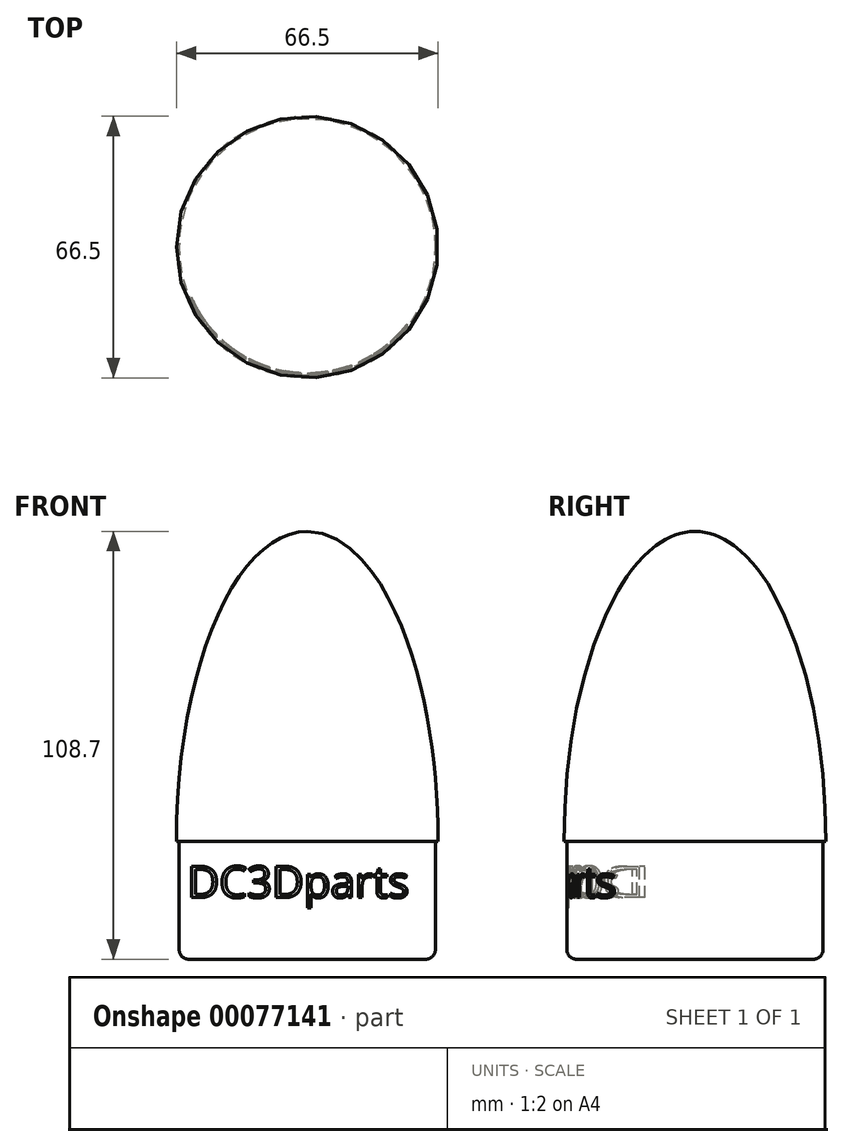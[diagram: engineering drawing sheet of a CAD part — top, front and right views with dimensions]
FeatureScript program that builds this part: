
annotation { "Feature Type Name" : "Feature", "Feature Type Description" : "" }
export const myFeature = defineFeature(function(context is Context, id is Id, definition is map)
    precondition{}
    {
        {
            var Q0;
            Q0=qCreatedBy(makeId("Front.planeOp"),FACE);
            var sketch = newSketch(context, id + "F0", { "sketchPlane" : qUnion([Q0])});
            skEllipticalArc(sketch, "E0", {});
            skLineSegment(sketch, "E1", {"start": v(0, 91.38) * mm, "end": v(0, -88.55) * mm, "construction": true});
            skPoint(sketch, "E1.startSnap0", {"position": v(0, 78.7) * mm});
            skLineSegment(sketch, "E2", {"start": v(-62.51, 0) * mm, "end": v(-32.55, 0) * mm, "construction": true});
            skLineSegment(sketch, "E3.top", {"start": v(0, -30) * mm, "end": v(-32.55, -30) * mm});
            skLineSegment(sketch, "E3.left", {"start": v(0, 0) * mm, "end": v(0, -30) * mm});
            skLineSegment(sketch, "E3.right", {"start": v(-32.55, 0) * mm, "end": v(-32.55, -30) * mm});
            skLineSegment(sketch, "E4", {"start": v(0, 78.7) * mm, "end": v(0, -30) * mm});
            skLineSegment(sketch, "E5.trimOffspring", {"start": v(0, 0) * mm, "end": v(63.8, 0) * mm, "construction": true});
            skLineSegment(sketch, "E6", {"start": v(-33.25, 0) * mm, "end": v(-32.55, 0) * mm});
            const initialGuessF0  = {"E0": [0, 0, 0, 1, 0.07870144238271146, 0.03325, 0, 1.5707963267948966]};
            skSetInitialGuess(sketch, initialGuessF0);
            skSolve(sketch);
        }
        {
            var Q0;
            {var subQ1=sQuery(id+"F0.wireOp",EDGE,"E0");Q0=makeQuery(id+"F0.imprint","IMPRINT",FACE,{"disambiguationData":[TD([[makeQuery(id+"F0.imprint","IMPRINT",EDGE,{"derivedFrom":subQ1}),1.0]])]});}
            var Q1;
            Q1=sQuery(id+"F0.wireOp",EDGE,"E1");
            revolve(context, id + "F1", {"entities" : qUnion([Q0]), "axis" : qUnion([Q1]), "revolveType" : RevolveType.FULL});
        }
        {
            var Q0;
            Q0=makeQuery(id+"F1.opRevolve","SWEPT_EDGE",EDGE,{"disambiguationData":[OSD([sQuery(id+"F0.wireOp",EDGE,"E3.top"),sQuery(id+"F0.wireOp",EDGE,"E3.right")])]});
            fillet(context, id + "F2", {"entities" : qUnion([Q0]), "radius" : 2.5 * mm, "tangentPropagation" : true, "allowEdgeOverflow" : false});
        }
        {
            var Q0;
            Q0=qCreatedBy(makeId("Front.planeOp"),FACE);
            cPlane(context, id + "F3", {"entities" : qUnion([Q0]), "cplaneType" : CPlaneType.OFFSET, "offset" : 40 * mm, "width" : 150 * mm, "height" : 150 * mm});
        }
        {
            var Q0;
            Q0=qCreatedBy(id+"F3.planeOp",FACE);
            var sketch = newSketch(context, id + "F4", { "sketchPlane" : qUnion([Q0])});
            skText(sketch, "E7", { "text": "DC3Dparts", "fontName": "OpenSans-Regular.ttf"});
            const initialGuessF4  = {"E7": [-0.03044, -0.01432, 1, 0, 0.008]};
            skSetInitialGuess(sketch, initialGuessF4);
            skSolve(sketch);
        }
        {
            var Q0;
            Q0=qCreatedBy(makeId("Front.planeOp"),FACE);
            var sketch = newSketch(context, id + "F5", { "sketchPlane" : qUnion([Q0])});
            skLineSegment(sketch, "E8.bottom", {"start": v(0, -18.53) * mm, "end": v(-32, -18.53) * mm});
            skLineSegment(sketch, "E8.top", {"start": v(0, -2.85) * mm, "end": v(-32, -2.85) * mm});
            skLineSegment(sketch, "E8.left", {"start": v(0, -18.53) * mm, "end": v(0, -2.85) * mm});
            skLineSegment(sketch, "E8.right", {"start": v(-32, -18.53) * mm, "end": v(-32, -2.85) * mm});
            skSolve(sketch);
        }
        {
            var Q0;
            Q0 = qSketchRegion(id + "F5", true);
            var Q1;
            Q1=sQuery(id+"F0.wireOp",EDGE,"E1");
            revolve(context, id + "F6", {"entities" : qUnion([Q0]), "axis" : qUnion([Q1]), "revolveType" : RevolveType.FULL});
        }
        {
            var Q0;
            Q0 = qSketchRegion(id + "F4", true);
            var Q1;
            Q1=qCreatedBy(makeId("Front.planeOp"),FACE);
            extrude(context, id + "F7", {"entities" : qUnion([Q0]), "endBound" : BoundingType.UP_TO_SURFACE, "oppositeDirection" : true, "depth" : 25 * mm, "endBoundEntityFace" : qUnion([Q1]), "offsetDistance" : 25 * mm});
        }
        {
            var Q0;
            Q0=makeQuery(id+"F6.opRevolve","SWEPT_BODY",BODY,{"disambiguationData":[OSD([sQuery(id+"F5.wireOp",EDGE,"E8.bottom"),sQuery(id+"F5.wireOp",EDGE,"E8.top"),sQuery(id+"F5.wireOp",EDGE,"E8.left"),sQuery(id+"F5.wireOp",EDGE,"E8.right")])]});
            var Q1;
            Q1=makeQuery(id+"F7.opExtrude","SWEPT_BODY",BODY,{"disambiguationData":[OSD([sQuery(id+"F4.wireOp",EDGE,"E7.sketch_text.stroke-0"),sQuery(id+"F4.wireOp",EDGE,"E7.sketch_text.stroke-1"),sQuery(id+"F4.wireOp",EDGE,"E7.sketch_text.stroke-2"),sQuery(id+"F4.wireOp",EDGE,"E7.sketch_text.stroke-3"),sQuery(id+"F4.wireOp",EDGE,"E7.sketch_text.stroke-4"),sQuery(id+"F4.wireOp",EDGE,"E7.sketch_text.stroke-5"),sQuery(id+"F4.wireOp",EDGE,"E7.sketch_text.stroke-6"),sQuery(id+"F4.wireOp",EDGE,"E7.sketch_text.stroke-7"),sQuery(id+"F4.wireOp",EDGE,"E7.sketch_text.stroke-8"),sQuery(id+"F4.wireOp",EDGE,"E7.sketch_text.stroke-9"),sQuery(id+"F4.wireOp",EDGE,"E7.sketch_text.stroke-10"),sQuery(id+"F4.wireOp",EDGE,"E7.sketch_text.stroke-11"),sQuery(id+"F4.wireOp",EDGE,"E7.sketch_text.stroke-12"),sQuery(id+"F4.wireOp",EDGE,"E7.sketch_text.stroke-13")])]});
            var Q2;
            Q2=makeQuery(id+"F7.opExtrude","SWEPT_BODY",BODY,{"disambiguationData":[OSD([sQuery(id+"F4.wireOp",EDGE,"E7.sketch_text.stroke-14"),sQuery(id+"F4.wireOp",EDGE,"E7.sketch_text.stroke-15"),sQuery(id+"F4.wireOp",EDGE,"E7.sketch_text.stroke-16"),sQuery(id+"F4.wireOp",EDGE,"E7.sketch_text.stroke-17"),sQuery(id+"F4.wireOp",EDGE,"E7.sketch_text.stroke-18"),sQuery(id+"F4.wireOp",EDGE,"E7.sketch_text.stroke-19"),sQuery(id+"F4.wireOp",EDGE,"E7.sketch_text.stroke-20"),sQuery(id+"F4.wireOp",EDGE,"E7.sketch_text.stroke-21"),sQuery(id+"F4.wireOp",EDGE,"E7.sketch_text.stroke-22"),sQuery(id+"F4.wireOp",EDGE,"E7.sketch_text.stroke-23"),sQuery(id+"F4.wireOp",EDGE,"E7.sketch_text.stroke-24"),sQuery(id+"F4.wireOp",EDGE,"E7.sketch_text.stroke-25"),sQuery(id+"F4.wireOp",EDGE,"E7.sketch_text.stroke-26"),sQuery(id+"F4.wireOp",EDGE,"E7.sketch_text.stroke-27"),sQuery(id+"F4.wireOp",EDGE,"E7.sketch_text.stroke-28")])]});
            var Q3;
            Q3=makeQuery(id+"F7.opExtrude","SWEPT_BODY",BODY,{"disambiguationData":[OSD([sQuery(id+"F4.wireOp",EDGE,"E7.sketch_text.stroke-29"),sQuery(id+"F4.wireOp",EDGE,"E7.sketch_text.stroke-30"),sQuery(id+"F4.wireOp",EDGE,"E7.sketch_text.stroke-31"),sQuery(id+"F4.wireOp",EDGE,"E7.sketch_text.stroke-32"),sQuery(id+"F4.wireOp",EDGE,"E7.sketch_text.stroke-33"),sQuery(id+"F4.wireOp",EDGE,"E7.sketch_text.stroke-34"),sQuery(id+"F4.wireOp",EDGE,"E7.sketch_text.stroke-35"),sQuery(id+"F4.wireOp",EDGE,"E7.sketch_text.stroke-36"),sQuery(id+"F4.wireOp",EDGE,"E7.sketch_text.stroke-37"),sQuery(id+"F4.wireOp",EDGE,"E7.sketch_text.stroke-38"),sQuery(id+"F4.wireOp",EDGE,"E7.sketch_text.stroke-39"),sQuery(id+"F4.wireOp",EDGE,"E7.sketch_text.stroke-40"),sQuery(id+"F4.wireOp",EDGE,"E7.sketch_text.stroke-41"),sQuery(id+"F4.wireOp",EDGE,"E7.sketch_text.stroke-42"),sQuery(id+"F4.wireOp",EDGE,"E7.sketch_text.stroke-43"),sQuery(id+"F4.wireOp",EDGE,"E7.sketch_text.stroke-44"),sQuery(id+"F4.wireOp",EDGE,"E7.sketch_text.stroke-45"),sQuery(id+"F4.wireOp",EDGE,"E7.sketch_text.stroke-46"),sQuery(id+"F4.wireOp",EDGE,"E7.sketch_text.stroke-47"),sQuery(id+"F4.wireOp",EDGE,"E7.sketch_text.stroke-48"),sQuery(id+"F4.wireOp",EDGE,"E7.sketch_text.stroke-49"),sQuery(id+"F4.wireOp",EDGE,"E7.sketch_text.stroke-50"),sQuery(id+"F4.wireOp",EDGE,"E7.sketch_text.stroke-51"),sQuery(id+"F4.wireOp",EDGE,"E7.sketch_text.stroke-52"),sQuery(id+"F4.wireOp",EDGE,"E7.sketch_text.stroke-53"),sQuery(id+"F4.wireOp",EDGE,"E7.sketch_text.stroke-54"),sQuery(id+"F4.wireOp",EDGE,"E7.sketch_text.stroke-55"),sQuery(id+"F4.wireOp",EDGE,"E7.sketch_text.stroke-56")])]});
            var Q4;
            Q4=makeQuery(id+"F7.opExtrude","SWEPT_BODY",BODY,{"disambiguationData":[OSD([sQuery(id+"F4.wireOp",EDGE,"E7.sketch_text.stroke-57"),sQuery(id+"F4.wireOp",EDGE,"E7.sketch_text.stroke-58"),sQuery(id+"F4.wireOp",EDGE,"E7.sketch_text.stroke-59"),sQuery(id+"F4.wireOp",EDGE,"E7.sketch_text.stroke-60"),sQuery(id+"F4.wireOp",EDGE,"E7.sketch_text.stroke-61"),sQuery(id+"F4.wireOp",EDGE,"E7.sketch_text.stroke-62"),sQuery(id+"F4.wireOp",EDGE,"E7.sketch_text.stroke-63"),sQuery(id+"F4.wireOp",EDGE,"E7.sketch_text.stroke-64"),sQuery(id+"F4.wireOp",EDGE,"E7.sketch_text.stroke-65"),sQuery(id+"F4.wireOp",EDGE,"E7.sketch_text.stroke-66"),sQuery(id+"F4.wireOp",EDGE,"E7.sketch_text.stroke-67"),sQuery(id+"F4.wireOp",EDGE,"E7.sketch_text.stroke-68"),sQuery(id+"F4.wireOp",EDGE,"E7.sketch_text.stroke-69"),sQuery(id+"F4.wireOp",EDGE,"E7.sketch_text.stroke-70")])]});
            var Q5;
            Q5=makeQuery(id+"F7.opExtrude","SWEPT_BODY",BODY,{"disambiguationData":[OSD([sQuery(id+"F4.wireOp",EDGE,"E7.sketch_text.stroke-71"),sQuery(id+"F4.wireOp",EDGE,"E7.sketch_text.stroke-72"),sQuery(id+"F4.wireOp",EDGE,"E7.sketch_text.stroke-73"),sQuery(id+"F4.wireOp",EDGE,"E7.sketch_text.stroke-74"),sQuery(id+"F4.wireOp",EDGE,"E7.sketch_text.stroke-75"),sQuery(id+"F4.wireOp",EDGE,"E7.sketch_text.stroke-76"),sQuery(id+"F4.wireOp",EDGE,"E7.sketch_text.stroke-77"),sQuery(id+"F4.wireOp",EDGE,"E7.sketch_text.stroke-78"),sQuery(id+"F4.wireOp",EDGE,"E7.sketch_text.stroke-79"),sQuery(id+"F4.wireOp",EDGE,"E7.sketch_text.stroke-80"),sQuery(id+"F4.wireOp",EDGE,"E7.sketch_text.stroke-81"),sQuery(id+"F4.wireOp",EDGE,"E7.sketch_text.stroke-82"),sQuery(id+"F4.wireOp",EDGE,"E7.sketch_text.stroke-83"),sQuery(id+"F4.wireOp",EDGE,"E7.sketch_text.stroke-84"),sQuery(id+"F4.wireOp",EDGE,"E7.sketch_text.stroke-85"),sQuery(id+"F4.wireOp",EDGE,"E7.sketch_text.stroke-86"),sQuery(id+"F4.wireOp",EDGE,"E7.sketch_text.stroke-87"),sQuery(id+"F4.wireOp",EDGE,"E7.sketch_text.stroke-88"),sQuery(id+"F4.wireOp",EDGE,"E7.sketch_text.stroke-89"),sQuery(id+"F4.wireOp",EDGE,"E7.sketch_text.stroke-90"),sQuery(id+"F4.wireOp",EDGE,"E7.sketch_text.stroke-91"),sQuery(id+"F4.wireOp",EDGE,"E7.sketch_text.stroke-92"),sQuery(id+"F4.wireOp",EDGE,"E7.sketch_text.stroke-93"),sQuery(id+"F4.wireOp",EDGE,"E7.sketch_text.stroke-94"),sQuery(id+"F4.wireOp",EDGE,"E7.sketch_text.stroke-95")])]});
            var Q6;
            Q6=makeQuery(id+"F7.opExtrude","SWEPT_BODY",BODY,{"disambiguationData":[OSD([sQuery(id+"F4.wireOp",EDGE,"E7.sketch_text.stroke-96"),sQuery(id+"F4.wireOp",EDGE,"E7.sketch_text.stroke-97"),sQuery(id+"F4.wireOp",EDGE,"E7.sketch_text.stroke-98"),sQuery(id+"F4.wireOp",EDGE,"E7.sketch_text.stroke-99"),sQuery(id+"F4.wireOp",EDGE,"E7.sketch_text.stroke-100"),sQuery(id+"F4.wireOp",EDGE,"E7.sketch_text.stroke-101"),sQuery(id+"F4.wireOp",EDGE,"E7.sketch_text.stroke-102"),sQuery(id+"F4.wireOp",EDGE,"E7.sketch_text.stroke-103"),sQuery(id+"F4.wireOp",EDGE,"E7.sketch_text.stroke-104"),sQuery(id+"F4.wireOp",EDGE,"E7.sketch_text.stroke-105"),sQuery(id+"F4.wireOp",EDGE,"E7.sketch_text.stroke-106"),sQuery(id+"F4.wireOp",EDGE,"E7.sketch_text.stroke-107"),sQuery(id+"F4.wireOp",EDGE,"E7.sketch_text.stroke-108"),sQuery(id+"F4.wireOp",EDGE,"E7.sketch_text.stroke-109"),sQuery(id+"F4.wireOp",EDGE,"E7.sketch_text.stroke-110"),sQuery(id+"F4.wireOp",EDGE,"E7.sketch_text.stroke-111"),sQuery(id+"F4.wireOp",EDGE,"E7.sketch_text.stroke-112"),sQuery(id+"F4.wireOp",EDGE,"E7.sketch_text.stroke-113"),sQuery(id+"F4.wireOp",EDGE,"E7.sketch_text.stroke-114"),sQuery(id+"F4.wireOp",EDGE,"E7.sketch_text.stroke-115"),sQuery(id+"F4.wireOp",EDGE,"E7.sketch_text.stroke-116"),sQuery(id+"F4.wireOp",EDGE,"E7.sketch_text.stroke-117"),sQuery(id+"F4.wireOp",EDGE,"E7.sketch_text.stroke-118"),sQuery(id+"F4.wireOp",EDGE,"E7.sketch_text.stroke-119"),sQuery(id+"F4.wireOp",EDGE,"E7.sketch_text.stroke-120"),sQuery(id+"F4.wireOp",EDGE,"E7.sketch_text.stroke-121"),sQuery(id+"F4.wireOp",EDGE,"E7.sketch_text.stroke-122")])]});
            var Q7;
            Q7=makeQuery(id+"F7.opExtrude","SWEPT_BODY",BODY,{"disambiguationData":[OSD([sQuery(id+"F4.wireOp",EDGE,"E7.sketch_text.stroke-123"),sQuery(id+"F4.wireOp",EDGE,"E7.sketch_text.stroke-124"),sQuery(id+"F4.wireOp",EDGE,"E7.sketch_text.stroke-125"),sQuery(id+"F4.wireOp",EDGE,"E7.sketch_text.stroke-126"),sQuery(id+"F4.wireOp",EDGE,"E7.sketch_text.stroke-127"),sQuery(id+"F4.wireOp",EDGE,"E7.sketch_text.stroke-128"),sQuery(id+"F4.wireOp",EDGE,"E7.sketch_text.stroke-129"),sQuery(id+"F4.wireOp",EDGE,"E7.sketch_text.stroke-130"),sQuery(id+"F4.wireOp",EDGE,"E7.sketch_text.stroke-131"),sQuery(id+"F4.wireOp",EDGE,"E7.sketch_text.stroke-132"),sQuery(id+"F4.wireOp",EDGE,"E7.sketch_text.stroke-133"),sQuery(id+"F4.wireOp",EDGE,"E7.sketch_text.stroke-134"),sQuery(id+"F4.wireOp",EDGE,"E7.sketch_text.stroke-135")])]});
            var Q8;
            Q8=makeQuery(id+"F7.opExtrude","SWEPT_BODY",BODY,{"disambiguationData":[OSD([sQuery(id+"F4.wireOp",EDGE,"E7.sketch_text.stroke-136"),sQuery(id+"F4.wireOp",EDGE,"E7.sketch_text.stroke-137"),sQuery(id+"F4.wireOp",EDGE,"E7.sketch_text.stroke-138"),sQuery(id+"F4.wireOp",EDGE,"E7.sketch_text.stroke-139"),sQuery(id+"F4.wireOp",EDGE,"E7.sketch_text.stroke-140"),sQuery(id+"F4.wireOp",EDGE,"E7.sketch_text.stroke-141"),sQuery(id+"F4.wireOp",EDGE,"E7.sketch_text.stroke-142"),sQuery(id+"F4.wireOp",EDGE,"E7.sketch_text.stroke-143"),sQuery(id+"F4.wireOp",EDGE,"E7.sketch_text.stroke-144"),sQuery(id+"F4.wireOp",EDGE,"E7.sketch_text.stroke-145"),sQuery(id+"F4.wireOp",EDGE,"E7.sketch_text.stroke-146"),sQuery(id+"F4.wireOp",EDGE,"E7.sketch_text.stroke-147"),sQuery(id+"F4.wireOp",EDGE,"E7.sketch_text.stroke-148"),sQuery(id+"F4.wireOp",EDGE,"E7.sketch_text.stroke-149"),sQuery(id+"F4.wireOp",EDGE,"E7.sketch_text.stroke-150"),sQuery(id+"F4.wireOp",EDGE,"E7.sketch_text.stroke-151"),sQuery(id+"F4.wireOp",EDGE,"E7.sketch_text.stroke-152"),sQuery(id+"F4.wireOp",EDGE,"E7.sketch_text.stroke-153"),sQuery(id+"F4.wireOp",EDGE,"E7.sketch_text.stroke-154")])]});
            var Q9;
            Q9=makeQuery(id+"F7.opExtrude","SWEPT_BODY",BODY,{"disambiguationData":[OSD([sQuery(id+"F4.wireOp",EDGE,"E7.sketch_text.stroke-155"),sQuery(id+"F4.wireOp",EDGE,"E7.sketch_text.stroke-156"),sQuery(id+"F4.wireOp",EDGE,"E7.sketch_text.stroke-157"),sQuery(id+"F4.wireOp",EDGE,"E7.sketch_text.stroke-158"),sQuery(id+"F4.wireOp",EDGE,"E7.sketch_text.stroke-159"),sQuery(id+"F4.wireOp",EDGE,"E7.sketch_text.stroke-160"),sQuery(id+"F4.wireOp",EDGE,"E7.sketch_text.stroke-161"),sQuery(id+"F4.wireOp",EDGE,"E7.sketch_text.stroke-162"),sQuery(id+"F4.wireOp",EDGE,"E7.sketch_text.stroke-163"),sQuery(id+"F4.wireOp",EDGE,"E7.sketch_text.stroke-164"),sQuery(id+"F4.wireOp",EDGE,"E7.sketch_text.stroke-165"),sQuery(id+"F4.wireOp",EDGE,"E7.sketch_text.stroke-166"),sQuery(id+"F4.wireOp",EDGE,"E7.sketch_text.stroke-167"),sQuery(id+"F4.wireOp",EDGE,"E7.sketch_text.stroke-168"),sQuery(id+"F4.wireOp",EDGE,"E7.sketch_text.stroke-169"),sQuery(id+"F4.wireOp",EDGE,"E7.sketch_text.stroke-170"),sQuery(id+"F4.wireOp",EDGE,"E7.sketch_text.stroke-171"),sQuery(id+"F4.wireOp",EDGE,"E7.sketch_text.stroke-172"),sQuery(id+"F4.wireOp",EDGE,"E7.sketch_text.stroke-173"),sQuery(id+"F4.wireOp",EDGE,"E7.sketch_text.stroke-174"),sQuery(id+"F4.wireOp",EDGE,"E7.sketch_text.stroke-175"),sQuery(id+"F4.wireOp",EDGE,"E7.sketch_text.stroke-176"),sQuery(id+"F4.wireOp",EDGE,"E7.sketch_text.stroke-177"),sQuery(id+"F4.wireOp",EDGE,"E7.sketch_text.stroke-178"),sQuery(id+"F4.wireOp",EDGE,"E7.sketch_text.stroke-179")])]});
            booleanBodies(context, id + "F8", {"operationType" : BooleanOperationType.SUBTRACTION, "tools" : qUnion([Q0]), "targets" : qUnion([Q1, Q2, Q3, Q4, Q5, Q6, Q7, Q8, Q9])});
        }
        {
            var Q0;
            Q0=makeQuery(id+"F7.opExtrude","SWEPT_BODY",BODY,{"disambiguationData":[OSD([sQuery(id+"F4.wireOp",EDGE,"E7.sketch_text.stroke-0"),sQuery(id+"F4.wireOp",EDGE,"E7.sketch_text.stroke-1"),sQuery(id+"F4.wireOp",EDGE,"E7.sketch_text.stroke-2"),sQuery(id+"F4.wireOp",EDGE,"E7.sketch_text.stroke-3"),sQuery(id+"F4.wireOp",EDGE,"E7.sketch_text.stroke-4"),sQuery(id+"F4.wireOp",EDGE,"E7.sketch_text.stroke-5"),sQuery(id+"F4.wireOp",EDGE,"E7.sketch_text.stroke-6"),sQuery(id+"F4.wireOp",EDGE,"E7.sketch_text.stroke-7"),sQuery(id+"F4.wireOp",EDGE,"E7.sketch_text.stroke-8"),sQuery(id+"F4.wireOp",EDGE,"E7.sketch_text.stroke-9"),sQuery(id+"F4.wireOp",EDGE,"E7.sketch_text.stroke-10"),sQuery(id+"F4.wireOp",EDGE,"E7.sketch_text.stroke-11"),sQuery(id+"F4.wireOp",EDGE,"E7.sketch_text.stroke-12"),sQuery(id+"F4.wireOp",EDGE,"E7.sketch_text.stroke-13")])]});
            var Q1;
            Q1=makeQuery(id+"F7.opExtrude","SWEPT_BODY",BODY,{"disambiguationData":[OSD([sQuery(id+"F4.wireOp",EDGE,"E7.sketch_text.stroke-14"),sQuery(id+"F4.wireOp",EDGE,"E7.sketch_text.stroke-15"),sQuery(id+"F4.wireOp",EDGE,"E7.sketch_text.stroke-16"),sQuery(id+"F4.wireOp",EDGE,"E7.sketch_text.stroke-17"),sQuery(id+"F4.wireOp",EDGE,"E7.sketch_text.stroke-18"),sQuery(id+"F4.wireOp",EDGE,"E7.sketch_text.stroke-19"),sQuery(id+"F4.wireOp",EDGE,"E7.sketch_text.stroke-20"),sQuery(id+"F4.wireOp",EDGE,"E7.sketch_text.stroke-21"),sQuery(id+"F4.wireOp",EDGE,"E7.sketch_text.stroke-22"),sQuery(id+"F4.wireOp",EDGE,"E7.sketch_text.stroke-23"),sQuery(id+"F4.wireOp",EDGE,"E7.sketch_text.stroke-24"),sQuery(id+"F4.wireOp",EDGE,"E7.sketch_text.stroke-25"),sQuery(id+"F4.wireOp",EDGE,"E7.sketch_text.stroke-26"),sQuery(id+"F4.wireOp",EDGE,"E7.sketch_text.stroke-27"),sQuery(id+"F4.wireOp",EDGE,"E7.sketch_text.stroke-28")])]});
            var Q2;
            Q2=makeQuery(id+"F7.opExtrude","SWEPT_BODY",BODY,{"disambiguationData":[OSD([sQuery(id+"F4.wireOp",EDGE,"E7.sketch_text.stroke-29"),sQuery(id+"F4.wireOp",EDGE,"E7.sketch_text.stroke-30"),sQuery(id+"F4.wireOp",EDGE,"E7.sketch_text.stroke-31"),sQuery(id+"F4.wireOp",EDGE,"E7.sketch_text.stroke-32"),sQuery(id+"F4.wireOp",EDGE,"E7.sketch_text.stroke-33"),sQuery(id+"F4.wireOp",EDGE,"E7.sketch_text.stroke-34"),sQuery(id+"F4.wireOp",EDGE,"E7.sketch_text.stroke-35"),sQuery(id+"F4.wireOp",EDGE,"E7.sketch_text.stroke-36"),sQuery(id+"F4.wireOp",EDGE,"E7.sketch_text.stroke-37"),sQuery(id+"F4.wireOp",EDGE,"E7.sketch_text.stroke-38"),sQuery(id+"F4.wireOp",EDGE,"E7.sketch_text.stroke-39"),sQuery(id+"F4.wireOp",EDGE,"E7.sketch_text.stroke-40"),sQuery(id+"F4.wireOp",EDGE,"E7.sketch_text.stroke-41"),sQuery(id+"F4.wireOp",EDGE,"E7.sketch_text.stroke-42"),sQuery(id+"F4.wireOp",EDGE,"E7.sketch_text.stroke-43"),sQuery(id+"F4.wireOp",EDGE,"E7.sketch_text.stroke-44"),sQuery(id+"F4.wireOp",EDGE,"E7.sketch_text.stroke-45"),sQuery(id+"F4.wireOp",EDGE,"E7.sketch_text.stroke-46"),sQuery(id+"F4.wireOp",EDGE,"E7.sketch_text.stroke-47"),sQuery(id+"F4.wireOp",EDGE,"E7.sketch_text.stroke-48"),sQuery(id+"F4.wireOp",EDGE,"E7.sketch_text.stroke-49"),sQuery(id+"F4.wireOp",EDGE,"E7.sketch_text.stroke-50"),sQuery(id+"F4.wireOp",EDGE,"E7.sketch_text.stroke-51"),sQuery(id+"F4.wireOp",EDGE,"E7.sketch_text.stroke-52"),sQuery(id+"F4.wireOp",EDGE,"E7.sketch_text.stroke-53"),sQuery(id+"F4.wireOp",EDGE,"E7.sketch_text.stroke-54"),sQuery(id+"F4.wireOp",EDGE,"E7.sketch_text.stroke-55"),sQuery(id+"F4.wireOp",EDGE,"E7.sketch_text.stroke-56")])]});
            var Q3;
            Q3=makeQuery(id+"F7.opExtrude","SWEPT_BODY",BODY,{"disambiguationData":[OSD([sQuery(id+"F4.wireOp",EDGE,"E7.sketch_text.stroke-57"),sQuery(id+"F4.wireOp",EDGE,"E7.sketch_text.stroke-58"),sQuery(id+"F4.wireOp",EDGE,"E7.sketch_text.stroke-59"),sQuery(id+"F4.wireOp",EDGE,"E7.sketch_text.stroke-60"),sQuery(id+"F4.wireOp",EDGE,"E7.sketch_text.stroke-61"),sQuery(id+"F4.wireOp",EDGE,"E7.sketch_text.stroke-62"),sQuery(id+"F4.wireOp",EDGE,"E7.sketch_text.stroke-63"),sQuery(id+"F4.wireOp",EDGE,"E7.sketch_text.stroke-64"),sQuery(id+"F4.wireOp",EDGE,"E7.sketch_text.stroke-65"),sQuery(id+"F4.wireOp",EDGE,"E7.sketch_text.stroke-66"),sQuery(id+"F4.wireOp",EDGE,"E7.sketch_text.stroke-67"),sQuery(id+"F4.wireOp",EDGE,"E7.sketch_text.stroke-68"),sQuery(id+"F4.wireOp",EDGE,"E7.sketch_text.stroke-69"),sQuery(id+"F4.wireOp",EDGE,"E7.sketch_text.stroke-70")])]});
            var Q4;
            Q4=makeQuery(id+"F7.opExtrude","SWEPT_BODY",BODY,{"disambiguationData":[OSD([sQuery(id+"F4.wireOp",EDGE,"E7.sketch_text.stroke-71"),sQuery(id+"F4.wireOp",EDGE,"E7.sketch_text.stroke-72"),sQuery(id+"F4.wireOp",EDGE,"E7.sketch_text.stroke-73"),sQuery(id+"F4.wireOp",EDGE,"E7.sketch_text.stroke-74"),sQuery(id+"F4.wireOp",EDGE,"E7.sketch_text.stroke-75"),sQuery(id+"F4.wireOp",EDGE,"E7.sketch_text.stroke-76"),sQuery(id+"F4.wireOp",EDGE,"E7.sketch_text.stroke-77"),sQuery(id+"F4.wireOp",EDGE,"E7.sketch_text.stroke-78"),sQuery(id+"F4.wireOp",EDGE,"E7.sketch_text.stroke-79"),sQuery(id+"F4.wireOp",EDGE,"E7.sketch_text.stroke-80"),sQuery(id+"F4.wireOp",EDGE,"E7.sketch_text.stroke-81"),sQuery(id+"F4.wireOp",EDGE,"E7.sketch_text.stroke-82"),sQuery(id+"F4.wireOp",EDGE,"E7.sketch_text.stroke-83"),sQuery(id+"F4.wireOp",EDGE,"E7.sketch_text.stroke-84"),sQuery(id+"F4.wireOp",EDGE,"E7.sketch_text.stroke-85"),sQuery(id+"F4.wireOp",EDGE,"E7.sketch_text.stroke-86"),sQuery(id+"F4.wireOp",EDGE,"E7.sketch_text.stroke-87"),sQuery(id+"F4.wireOp",EDGE,"E7.sketch_text.stroke-88"),sQuery(id+"F4.wireOp",EDGE,"E7.sketch_text.stroke-89"),sQuery(id+"F4.wireOp",EDGE,"E7.sketch_text.stroke-90"),sQuery(id+"F4.wireOp",EDGE,"E7.sketch_text.stroke-91"),sQuery(id+"F4.wireOp",EDGE,"E7.sketch_text.stroke-92"),sQuery(id+"F4.wireOp",EDGE,"E7.sketch_text.stroke-93"),sQuery(id+"F4.wireOp",EDGE,"E7.sketch_text.stroke-94"),sQuery(id+"F4.wireOp",EDGE,"E7.sketch_text.stroke-95")])]});
            var Q5;
            Q5=makeQuery(id+"F7.opExtrude","SWEPT_BODY",BODY,{"disambiguationData":[OSD([sQuery(id+"F4.wireOp",EDGE,"E7.sketch_text.stroke-96"),sQuery(id+"F4.wireOp",EDGE,"E7.sketch_text.stroke-97"),sQuery(id+"F4.wireOp",EDGE,"E7.sketch_text.stroke-98"),sQuery(id+"F4.wireOp",EDGE,"E7.sketch_text.stroke-99"),sQuery(id+"F4.wireOp",EDGE,"E7.sketch_text.stroke-100"),sQuery(id+"F4.wireOp",EDGE,"E7.sketch_text.stroke-101"),sQuery(id+"F4.wireOp",EDGE,"E7.sketch_text.stroke-102"),sQuery(id+"F4.wireOp",EDGE,"E7.sketch_text.stroke-103"),sQuery(id+"F4.wireOp",EDGE,"E7.sketch_text.stroke-104"),sQuery(id+"F4.wireOp",EDGE,"E7.sketch_text.stroke-105"),sQuery(id+"F4.wireOp",EDGE,"E7.sketch_text.stroke-106"),sQuery(id+"F4.wireOp",EDGE,"E7.sketch_text.stroke-107"),sQuery(id+"F4.wireOp",EDGE,"E7.sketch_text.stroke-108"),sQuery(id+"F4.wireOp",EDGE,"E7.sketch_text.stroke-109"),sQuery(id+"F4.wireOp",EDGE,"E7.sketch_text.stroke-110"),sQuery(id+"F4.wireOp",EDGE,"E7.sketch_text.stroke-111"),sQuery(id+"F4.wireOp",EDGE,"E7.sketch_text.stroke-112"),sQuery(id+"F4.wireOp",EDGE,"E7.sketch_text.stroke-113"),sQuery(id+"F4.wireOp",EDGE,"E7.sketch_text.stroke-114"),sQuery(id+"F4.wireOp",EDGE,"E7.sketch_text.stroke-115"),sQuery(id+"F4.wireOp",EDGE,"E7.sketch_text.stroke-116"),sQuery(id+"F4.wireOp",EDGE,"E7.sketch_text.stroke-117"),sQuery(id+"F4.wireOp",EDGE,"E7.sketch_text.stroke-118"),sQuery(id+"F4.wireOp",EDGE,"E7.sketch_text.stroke-119"),sQuery(id+"F4.wireOp",EDGE,"E7.sketch_text.stroke-120"),sQuery(id+"F4.wireOp",EDGE,"E7.sketch_text.stroke-121"),sQuery(id+"F4.wireOp",EDGE,"E7.sketch_text.stroke-122")])]});
            var Q6;
            Q6=makeQuery(id+"F7.opExtrude","SWEPT_BODY",BODY,{"disambiguationData":[OSD([sQuery(id+"F4.wireOp",EDGE,"E7.sketch_text.stroke-123"),sQuery(id+"F4.wireOp",EDGE,"E7.sketch_text.stroke-124"),sQuery(id+"F4.wireOp",EDGE,"E7.sketch_text.stroke-125"),sQuery(id+"F4.wireOp",EDGE,"E7.sketch_text.stroke-126"),sQuery(id+"F4.wireOp",EDGE,"E7.sketch_text.stroke-127"),sQuery(id+"F4.wireOp",EDGE,"E7.sketch_text.stroke-128"),sQuery(id+"F4.wireOp",EDGE,"E7.sketch_text.stroke-129"),sQuery(id+"F4.wireOp",EDGE,"E7.sketch_text.stroke-130"),sQuery(id+"F4.wireOp",EDGE,"E7.sketch_text.stroke-131"),sQuery(id+"F4.wireOp",EDGE,"E7.sketch_text.stroke-132"),sQuery(id+"F4.wireOp",EDGE,"E7.sketch_text.stroke-133"),sQuery(id+"F4.wireOp",EDGE,"E7.sketch_text.stroke-134"),sQuery(id+"F4.wireOp",EDGE,"E7.sketch_text.stroke-135")])]});
            var Q7;
            Q7=makeQuery(id+"F7.opExtrude","SWEPT_BODY",BODY,{"disambiguationData":[OSD([sQuery(id+"F4.wireOp",EDGE,"E7.sketch_text.stroke-136"),sQuery(id+"F4.wireOp",EDGE,"E7.sketch_text.stroke-137"),sQuery(id+"F4.wireOp",EDGE,"E7.sketch_text.stroke-138"),sQuery(id+"F4.wireOp",EDGE,"E7.sketch_text.stroke-139"),sQuery(id+"F4.wireOp",EDGE,"E7.sketch_text.stroke-140"),sQuery(id+"F4.wireOp",EDGE,"E7.sketch_text.stroke-141"),sQuery(id+"F4.wireOp",EDGE,"E7.sketch_text.stroke-142"),sQuery(id+"F4.wireOp",EDGE,"E7.sketch_text.stroke-143"),sQuery(id+"F4.wireOp",EDGE,"E7.sketch_text.stroke-144"),sQuery(id+"F4.wireOp",EDGE,"E7.sketch_text.stroke-145"),sQuery(id+"F4.wireOp",EDGE,"E7.sketch_text.stroke-146"),sQuery(id+"F4.wireOp",EDGE,"E7.sketch_text.stroke-147"),sQuery(id+"F4.wireOp",EDGE,"E7.sketch_text.stroke-148"),sQuery(id+"F4.wireOp",EDGE,"E7.sketch_text.stroke-149"),sQuery(id+"F4.wireOp",EDGE,"E7.sketch_text.stroke-150"),sQuery(id+"F4.wireOp",EDGE,"E7.sketch_text.stroke-151"),sQuery(id+"F4.wireOp",EDGE,"E7.sketch_text.stroke-152"),sQuery(id+"F4.wireOp",EDGE,"E7.sketch_text.stroke-153"),sQuery(id+"F4.wireOp",EDGE,"E7.sketch_text.stroke-154")])]});
            var Q8;
            Q8=makeQuery(id+"F7.opExtrude","SWEPT_BODY",BODY,{"disambiguationData":[OSD([sQuery(id+"F4.wireOp",EDGE,"E7.sketch_text.stroke-155"),sQuery(id+"F4.wireOp",EDGE,"E7.sketch_text.stroke-156"),sQuery(id+"F4.wireOp",EDGE,"E7.sketch_text.stroke-157"),sQuery(id+"F4.wireOp",EDGE,"E7.sketch_text.stroke-158"),sQuery(id+"F4.wireOp",EDGE,"E7.sketch_text.stroke-159"),sQuery(id+"F4.wireOp",EDGE,"E7.sketch_text.stroke-160"),sQuery(id+"F4.wireOp",EDGE,"E7.sketch_text.stroke-161"),sQuery(id+"F4.wireOp",EDGE,"E7.sketch_text.stroke-162"),sQuery(id+"F4.wireOp",EDGE,"E7.sketch_text.stroke-163"),sQuery(id+"F4.wireOp",EDGE,"E7.sketch_text.stroke-164"),sQuery(id+"F4.wireOp",EDGE,"E7.sketch_text.stroke-165"),sQuery(id+"F4.wireOp",EDGE,"E7.sketch_text.stroke-166"),sQuery(id+"F4.wireOp",EDGE,"E7.sketch_text.stroke-167"),sQuery(id+"F4.wireOp",EDGE,"E7.sketch_text.stroke-168"),sQuery(id+"F4.wireOp",EDGE,"E7.sketch_text.stroke-169"),sQuery(id+"F4.wireOp",EDGE,"E7.sketch_text.stroke-170"),sQuery(id+"F4.wireOp",EDGE,"E7.sketch_text.stroke-171"),sQuery(id+"F4.wireOp",EDGE,"E7.sketch_text.stroke-172"),sQuery(id+"F4.wireOp",EDGE,"E7.sketch_text.stroke-173"),sQuery(id+"F4.wireOp",EDGE,"E7.sketch_text.stroke-174"),sQuery(id+"F4.wireOp",EDGE,"E7.sketch_text.stroke-175"),sQuery(id+"F4.wireOp",EDGE,"E7.sketch_text.stroke-176"),sQuery(id+"F4.wireOp",EDGE,"E7.sketch_text.stroke-177"),sQuery(id+"F4.wireOp",EDGE,"E7.sketch_text.stroke-178"),sQuery(id+"F4.wireOp",EDGE,"E7.sketch_text.stroke-179")])]});
            var Q9;
            Q9=makeQuery(id+"F1.opRevolve","SWEPT_BODY",BODY,{"disambiguationData":[OSD([sQuery(id+"F0.wireOp",EDGE,"E0"),sQuery(id+"F0.wireOp",EDGE,"E3.top"),sQuery(id+"F0.wireOp",EDGE,"E3.right"),sQuery(id+"F0.wireOp",EDGE,"E4"),sQuery(id+"F0.wireOp",EDGE,"E6")])]});
            booleanBodies(context, id + "F9", {"operationType" : BooleanOperationType.SUBTRACTION, "tools" : qUnion([Q0, Q1, Q2, Q3, Q4, Q5, Q6, Q7, Q8]), "targets" : qUnion([Q9])});
        }
    });
